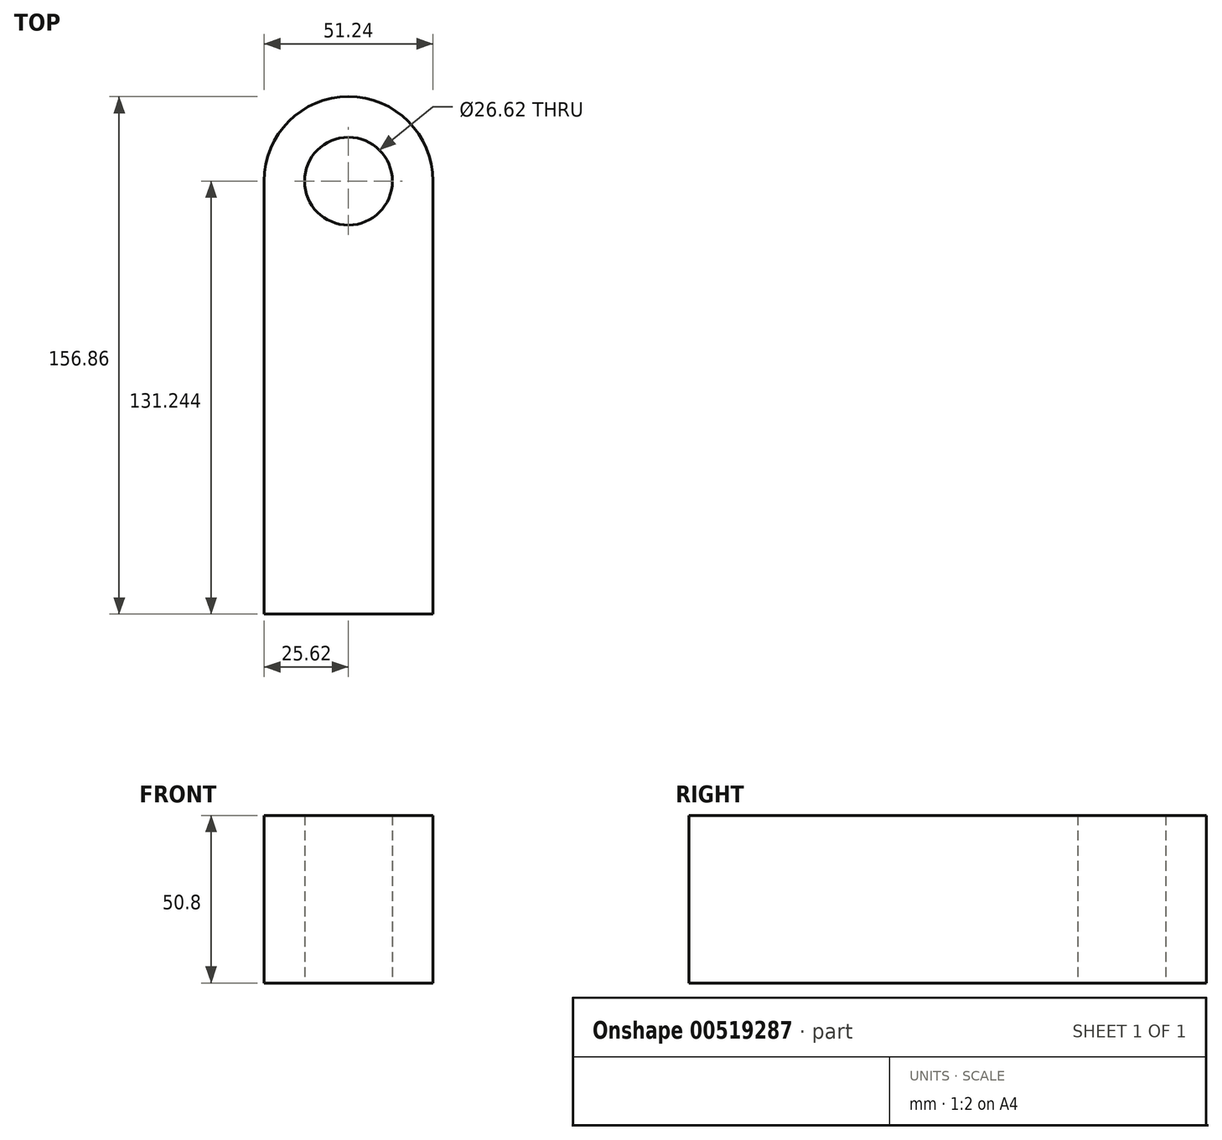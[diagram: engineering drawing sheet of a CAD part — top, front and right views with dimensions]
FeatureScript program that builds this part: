
annotation { "Feature Type Name" : "Feature", "Feature Type Description" : "" }
export const myFeature = defineFeature(function(context is Context, id is Id, definition is map)
    precondition{}
    {
        {
            var Q0;
            Q0=qCreatedBy(makeId("Top.planeOp"),FACE);
            var sketch = newSketch(context, id + "F0", { "sketchPlane" : qUnion([Q0])});
            skLineSegment(sketch, "E0.top", {"start": v(25.62, -65.62) * mm, "end": v(-25.62, -65.62) * mm});
            skLineSegment(sketch, "E0.left", {"start": v(25.62, 65.62) * mm, "end": v(25.62, -65.62) * mm});
            skLineSegment(sketch, "E0.right", {"start": v(-25.62, 65.62) * mm, "end": v(-25.62, -65.62) * mm});
            skPoint(sketch, "E0.middle", {"position": v(0, 0) * mm});
            skArc(sketch, "E1", {"start": v(25.62, 65.62) * mm, "mid": v(0, 91.24) * mm, "end": v(-25.62, 65.62) * mm});
            skCircle(sketch, "E2", {"center": v(0, 65.62) * mm, "radius": 13.31 * mm});
            skSolve(sketch);
        }
        {
            var Q0;
            Q0=makeQuery(id+"F0.imprint","IMPRINT",FACE,{"disambiguationData":[TD([[makeQuery(id+"F0.imprint","IMPRINT",EDGE,{"derivedFrom":sQuery(id+"F0.wireOp",EDGE,"E0.top")}),-1.0]])]});
            extrude(context, id + "F1", {"entities" : qUnion([Q0]), "depth" : 50.8 * mm, "offsetDistance" : 25.4 * mm});
        }
    });
